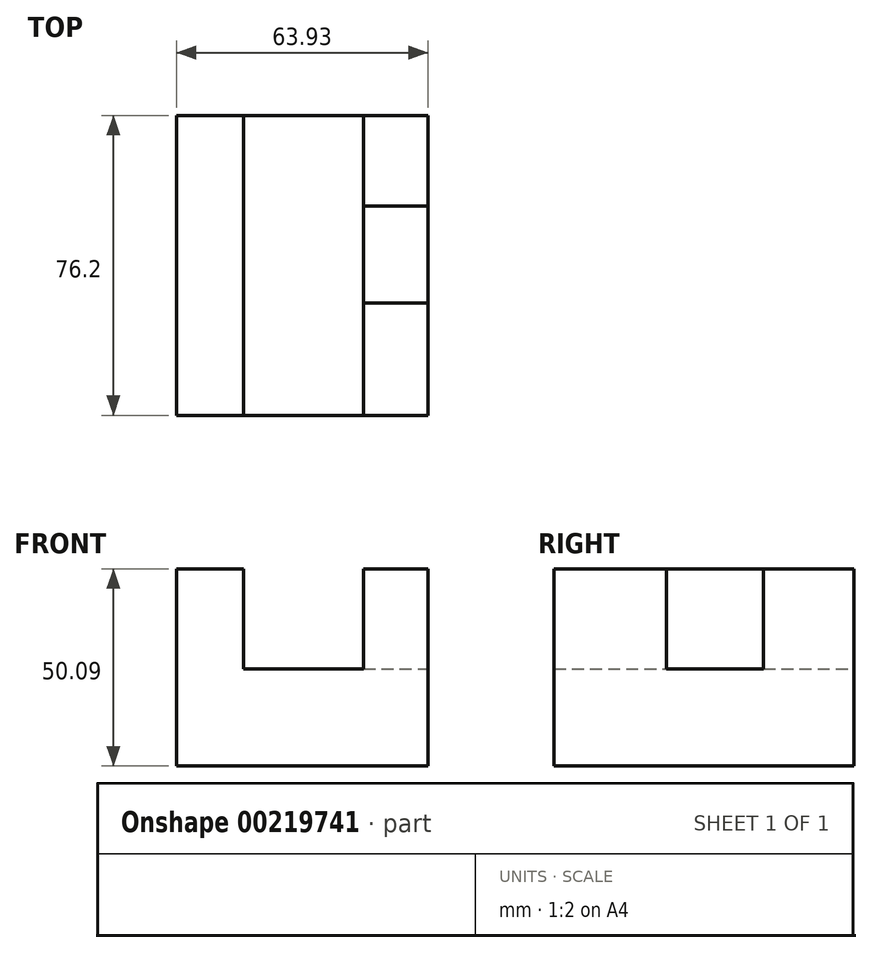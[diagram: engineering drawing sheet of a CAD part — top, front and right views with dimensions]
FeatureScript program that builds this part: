
annotation { "Feature Type Name" : "Feature", "Feature Type Description" : "" }
export const myFeature = defineFeature(function(context is Context, id is Id, definition is map)
    precondition{}
    {
        {
            var Q0;
            Q0=qCreatedBy(makeId("Front.planeOp"),FACE);
            var sketch = newSketch(context, id + "F0", { "sketchPlane" : qUnion([Q0])});
            skLineSegment(sketch, "E0.bottom", {"start": v(0, 0) * mm, "end": v(63.93, 0) * mm});
            skLineSegment(sketch, "E0.top", {"start": v(0, 50.1) * mm, "end": v(17.05, 50.1) * mm});
            skLineSegment(sketch, "E0.left", {"start": v(0, 0) * mm, "end": v(0, 50.1) * mm});
            skLineSegment(sketch, "E0.right", {"start": v(63.93, 0) * mm, "end": v(63.93, 50.1) * mm});
            skLineSegment(sketch, "E1.top", {"start": v(17.05, 24.7) * mm, "end": v(47.54, 24.7) * mm});
            skLineSegment(sketch, "E1.left", {"start": v(17.05, 50.1) * mm, "end": v(17.05, 24.7) * mm});
            skLineSegment(sketch, "E1.right", {"start": v(47.54, 50.1) * mm, "end": v(47.54, 24.7) * mm});
            skLineSegment(sketch, "E2.trimOffspring", {"start": v(47.54, 50.1) * mm, "end": v(63.93, 50.1) * mm});
            skSolve(sketch);
        }
        {
            var Q0;
            Q0 = qSketchRegion(id + "F0", true);
            extrude(context, id + "F1", {"entities" : qUnion([Q0]), "depth" : 76.2 * mm});
        }
        {
            var Q0;
            Q0=makeQuery(id+"F1.opExtrude","SWEPT_FACE",FACE,{"disambiguationData":[OSD([sQuery(id+"F0.wireOp",EDGE,"E2.trimOffspring")])]});
            var sketch = newSketch(context, id + "F2", { "sketchPlane" : qUnion([Q0])});
            skLineSegment(sketch, "E3.bottom", {"start": v(47.54, -47.61) * mm, "end": v(63.93, -47.61) * mm});
            skLineSegment(sketch, "E3.top", {"start": v(47.54, -22.97) * mm, "end": v(63.93, -22.97) * mm});
            skLineSegment(sketch, "E3.left", {"start": v(47.54, -47.61) * mm, "end": v(47.54, -22.97) * mm});
            skLineSegment(sketch, "E3.right", {"start": v(63.93, -47.61) * mm, "end": v(63.93, -22.97) * mm});
            skSolve(sketch);
        }
        {
            var Q0;
            Q0 = qSketchRegion(id + "F2", true);
            extrude(context, id + "F3", {"entities" : qUnion([Q0]), "operationType" : NewBodyOperationType.REMOVE, "oppositeDirection" : true, "depth" : 25.4 * mm});
        }
    });
